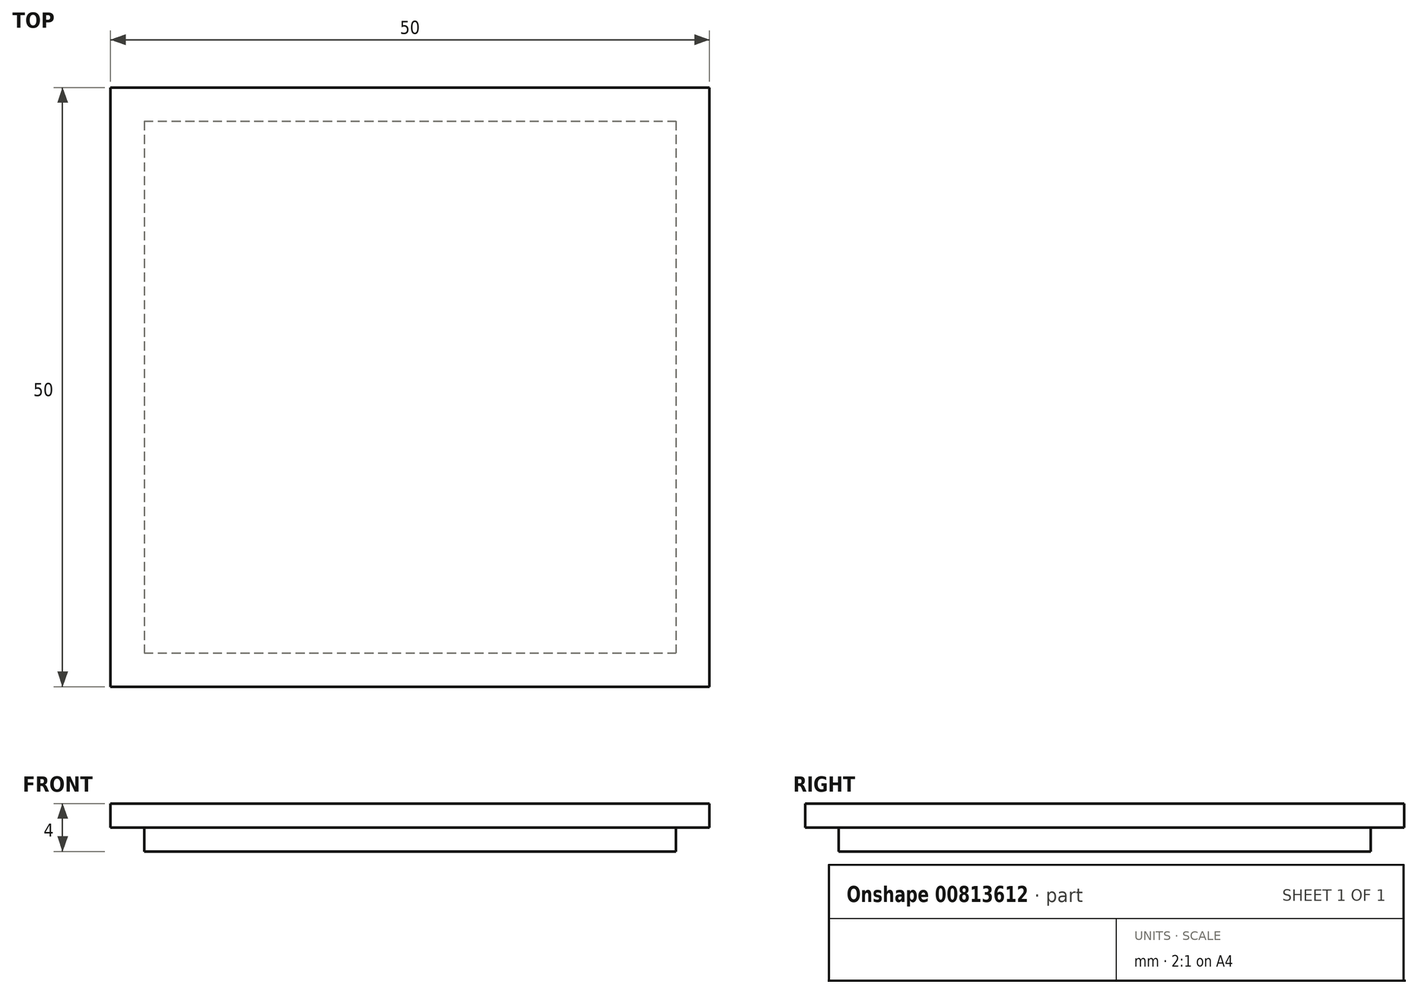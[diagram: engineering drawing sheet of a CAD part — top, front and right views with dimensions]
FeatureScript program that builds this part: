
annotation { "Feature Type Name" : "Feature", "Feature Type Description" : "" }
export const myFeature = defineFeature(function(context is Context, id is Id, definition is map)
    precondition{}
    {
        {
            var Q0;
            Q0=qCreatedBy(makeId("Top.planeOp"),FACE);
            var sketch = newSketch(context, id + "F0", { "sketchPlane" : qUnion([Q0])});
            skLineSegment(sketch, "E0.bottom", {"start": v(-22.2, 22.2) * mm, "end": v(22.2, 22.2) * mm});
            skLineSegment(sketch, "E0.top", {"start": v(-22.2, -22.2) * mm, "end": v(22.2, -22.2) * mm});
            skLineSegment(sketch, "E0.left", {"start": v(-22.2, 22.2) * mm, "end": v(-22.2, -22.2) * mm});
            skLineSegment(sketch, "E0.right", {"start": v(22.2, 22.2) * mm, "end": v(22.2, -22.2) * mm});
            skPoint(sketch, "E0.middle", {"position": v(0, 0) * mm});
            skLineSegment(sketch, "E1.bottom", {"start": v(25, 25) * mm, "end": v(-25, 25) * mm});
            skLineSegment(sketch, "E1.top", {"start": v(25, -25) * mm, "end": v(-25, -25) * mm});
            skLineSegment(sketch, "E1.left", {"start": v(25, 25) * mm, "end": v(25, -25) * mm});
            skLineSegment(sketch, "E1.right", {"start": v(-25, 25) * mm, "end": v(-25, -25) * mm});
            skSolve(sketch);
        }
        {
            var Q0;
            Q0=makeQuery(id+"F0.imprint","IMPRINT",FACE,{"disambiguationData":[TD([[makeQuery(id+"F0.imprint","IMPRINT",EDGE,{"derivedFrom":sQuery(id+"F0.wireOp",EDGE,"E0.bottom")}),-1.0]])]});
            extrude(context, id + "F1", {"entities" : qUnion([Q0]), "oppositeDirection" : true, "depth" : 2 * mm, "offsetDistance" : 25 * mm});
        }
        {
            var Q0;
            Q0 = qSketchRegion(id + "F0", true);
            var Q1;
            Q1=makeQuery(id+"F1.opExtrude","CAP_FACE",FACE,{"disambiguationData":[OSD([sQuery(id+"F0.wireOp",EDGE,"E0.bottom"),sQuery(id+"F0.wireOp",EDGE,"E0.top"),sQuery(id+"F0.wireOp",EDGE,"E0.left"),sQuery(id+"F0.wireOp",EDGE,"E0.right")])],"isStart":true});
            extrude(context, id + "F2", {"entities" : qUnion([Q0, Q1]), "operationType" : NewBodyOperationType.ADD, "depth" : 2 * mm, "offsetDistance" : 25 * mm});
        }
    });
